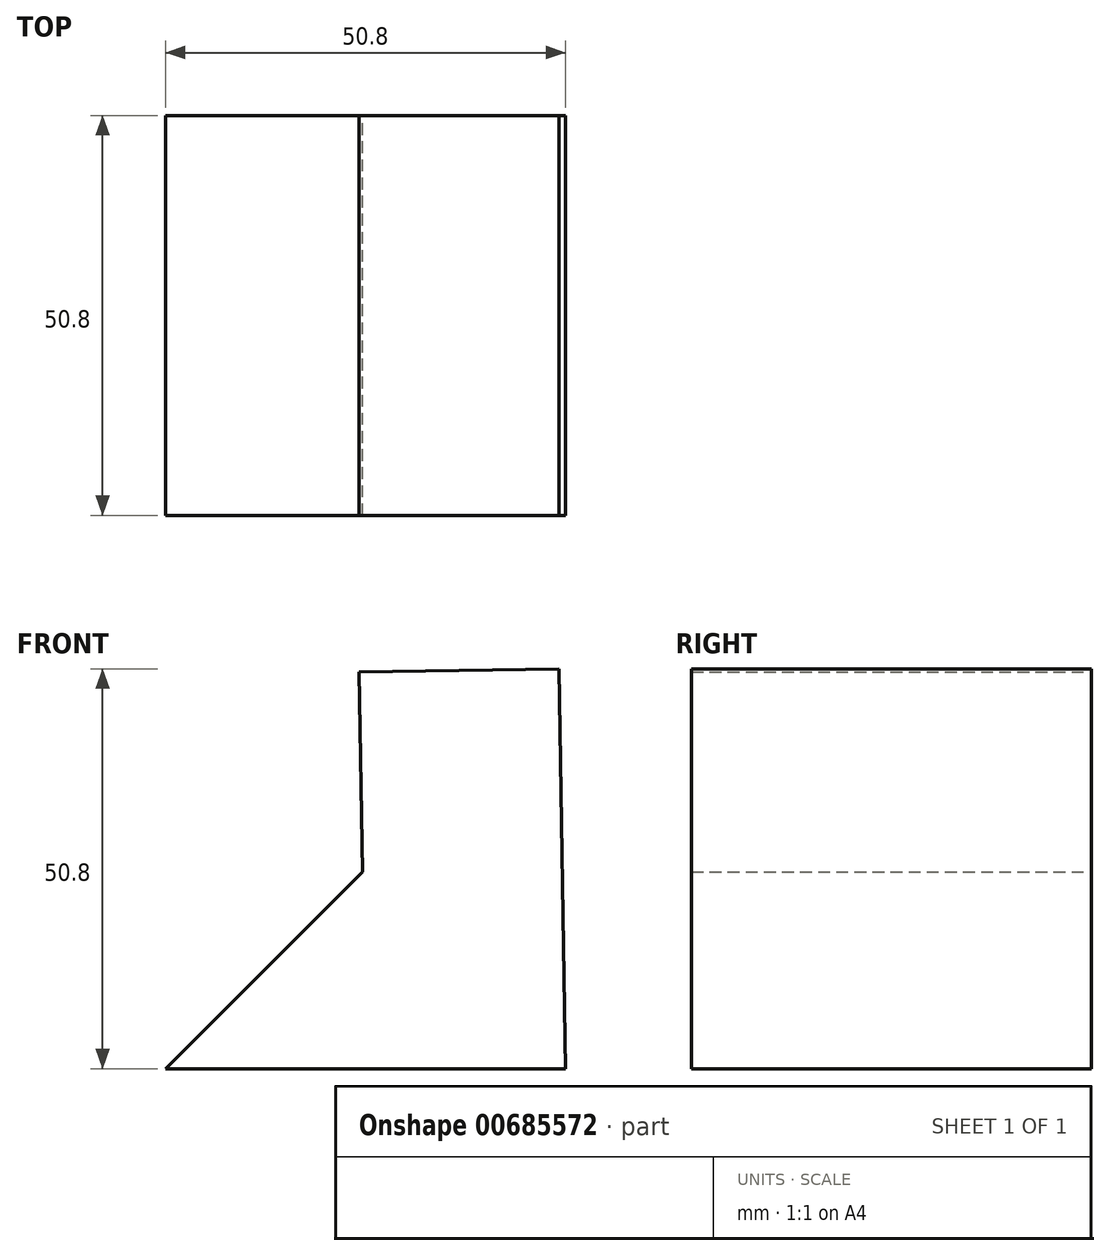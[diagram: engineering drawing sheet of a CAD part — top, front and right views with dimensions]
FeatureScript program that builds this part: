
annotation { "Feature Type Name" : "Feature", "Feature Type Description" : "" }
export const myFeature = defineFeature(function(context is Context, id is Id, definition is map)
    precondition{}
    {
        {
            var Q0;
            Q0=qCreatedBy(makeId("Front.planeOp"),FACE);
            var sketch = newSketch(context, id + "F0", { "sketchPlane" : qUnion([Q0])});
            skLineSegment(sketch, "E0", {"start": v(-49.99, -13.1) * mm, "end": v(0.81, -13.1) * mm});
            skLineSegment(sketch, "E1", {"start": v(0.81, -13.1) * mm, "end": v(0, 37.69) * mm});
            skLineSegment(sketch, "E2", {"start": v(0, 37.69) * mm, "end": v(-25.4, 37.28) * mm});
            skLineSegment(sketch, "E3", {"start": v(-25.4, 37.28) * mm, "end": v(-24.99, 11.88) * mm});
            skLineSegment(sketch, "E4", {"start": v(-24.99, 11.88) * mm, "end": v(-49.99, -13.1) * mm});
            skSolve(sketch);
        }
        {
            var Q0;
            Q0=makeQuery(id+"F0.imprint","IMPRINT",FACE,{"disambiguationData":[TD([[makeQuery(id+"F0.imprint","IMPRINT",EDGE,{"derivedFrom":sQuery(id+"F0.wireOp",EDGE,"E0")}),1.0]])]});
            extrude(context, id + "F1", {"entities" : qUnion([Q0]), "depth" : 50.8 * mm, "offsetDistance" : 25.4 * mm});
        }
    });
